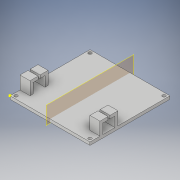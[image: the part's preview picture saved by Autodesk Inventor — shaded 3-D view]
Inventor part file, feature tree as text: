
AUTODESK INVENTOR PART (.ipt)
format: ipt  version: 2018 (Build 220112000, 112)  size: 162,816 bytes
history: native  units: mm
features: sketch x4, extrude x3, mirror x2, plane x1
ambient origin geometry x8: Origin, YZ Plane, XZ Plane, XY Plane, X Axis, Y Axis, Z Axis, Center Point
bodies: Solid1 (feature_tree)
feature tree (10):
  extrude  "Extrusion1"  Depth=80.0mm
  sketch  "Sketch2"  dims[d2=3.0mm d3=0.0mm d4=3.0mm]
  sketch  "Sketch3"  dims[d5=3.0mm d6=10.0mm]
  plane  "Work Plane1"
  extrude  "Extrusion2"  Depth=3.0mm
  mirror  "Mirror1"
  extrude  "Extrusion3"  Depth=10.0mm
  mirror  "Mirror2"
  sketch  "Sketch1"  dims[d0=80.0mm d1=80.0mm]
  sketch  "Sketch4"  dims[d7=12.0mm d8=10.0mm d9=3.0mm d10=5.0mm d11=5.0mm d12=3.0mm d13=10.0mm d14=0.0mm d15=3.2mm d16=3.0mm d17=3.0mm d18=3.0mm d19=10.0mm d20=0.0mm]
